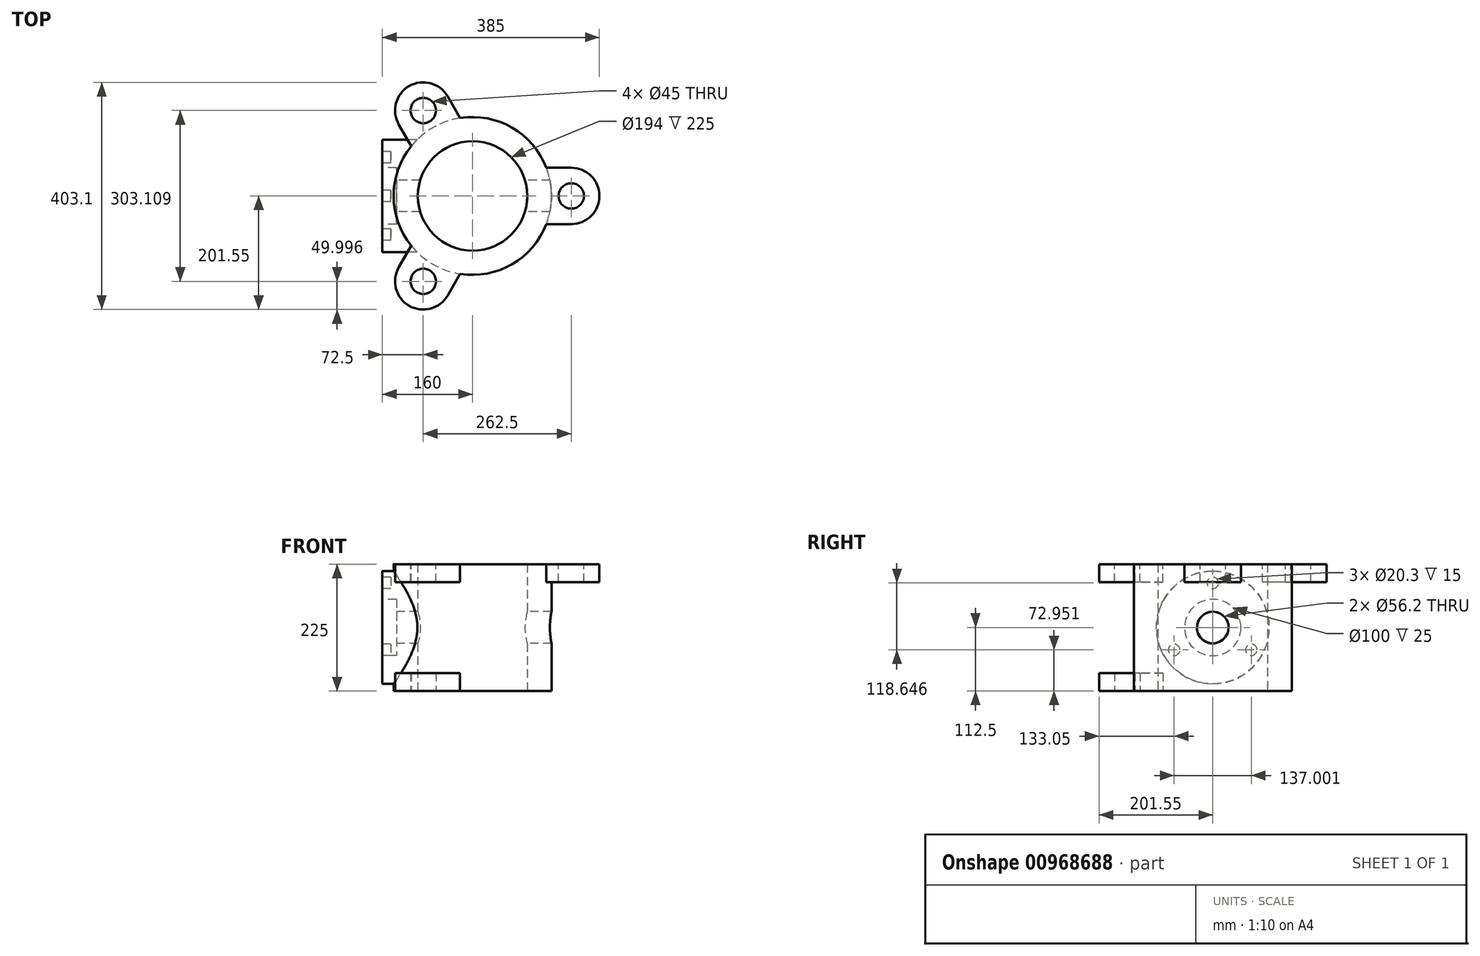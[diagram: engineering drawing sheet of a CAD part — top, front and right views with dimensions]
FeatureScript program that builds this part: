
annotation { "Feature Type Name" : "Feature", "Feature Type Description" : "" }
export const myFeature = defineFeature(function(context is Context, id is Id, definition is map)
    precondition{}
    {
        {
            var Q0;
            Q0=qCreatedBy(makeId("Top.planeOp"),FACE);
            var sketch = newSketch(context, id + "F0", { "sketchPlane" : qUnion([Q0])});
            skCircle(sketch, "E0", {"center": v(0, 0) * mm, "radius": 97 * mm});
            skCircle(sketch, "E1", {"center": v(0, 0) * mm, "radius": 140 * mm});
            skSolve(sketch);
        }
        {
            var Q0;
            Q0=makeQuery(id+"F0.imprint","IMPRINT",FACE,{"disambiguationData":[TD([[makeQuery(id+"F0.imprint","IMPRINT",EDGE,{"derivedFrom":sQuery(id+"F0.wireOp",EDGE,"E0")}),-1.0]])]});
            extrude(context, id + "F1", {"entities" : qUnion([Q0]), "endBound" : BoundingType.SYMMETRIC, "depth" : 225 * mm, "offsetDistance" : 25 * mm});
        }
        {
            var Q0;
            Q0=makeQuery(id+"F1.opExtrude","CAP_FACE",FACE,{"disambiguationData":[OSD([sQuery(id+"F0.wireOp",EDGE,"E0"),sQuery(id+"F0.wireOp",EDGE,"E1")])],"isStart":true});
            var sketch = newSketch(context, id + "F2", { "sketchPlane" : qUnion([Q0])});
            skLineSegment(sketch, "E2.0", {"start": v(-130.8, 126.55) * mm, "end": v(-108.68, 88.25) * mm});
            skArc(sketch, "E3.0", {"start": v(-130.8, 126.55) * mm, "mid": v(-112.5, 194.86) * mm, "end": v(-44.2, 176.55) * mm});
            skLineSegment(sketch, "E4.0", {"start": v(-44.2, 176.55) * mm, "end": v(-22.08, 138.25) * mm});
            skCircle(sketch, "E5.0", {"center": v(0, 0) * mm, "radius": 140 * mm});
            skCircle(sketch, "E6.0", {"center": v(-87.5, 151.55) * mm, "radius": 22.5 * mm});
            skSolve(sketch);
        }
        {
            var Q0;
            {var subQ1=sQuery(id+"F2FDXNzwOm2uh5E_1.2.F2.wireOp",EDGE,"E2.0");Q0=makeQuery(id+"F2FDXNzwOm2uh5E_1.2.F2.imprint","IMPRINT",FACE,{"disambiguationData":[TD([[makeQuery(id+"F2FDXNzwOm2uh5E_1.2.F2.imprint","IMPRINT",EDGE,{"derivedFrom":subQ1}),1.0]])]});}
            var Q1;
            {var subQ1=sQuery(id+"F2.wireOp",EDGE,"E2.0");Q1=makeQuery(id+"F2.imprint","IMPRINT",FACE,{"disambiguationData":[TD([[makeQuery(id+"F2.imprint","IMPRINT",EDGE,{"derivedFrom":subQ1}),1.0]])]});}
            var Q2;
            {var subQ1=sQuery(id+"F2FDXNzwOm2uh5E_1.1.F2.wireOp",EDGE,"E2.0");Q2=makeQuery(id+"F2FDXNzwOm2uh5E_1.1.F2.imprint","IMPRINT",FACE,{"disambiguationData":[TD([[makeQuery(id+"F2FDXNzwOm2uh5E_1.1.F2.imprint","IMPRINT",EDGE,{"derivedFrom":subQ1}),1.0]])]});}
            extrude(context, id + "F3", {"entities" : qUnion([Q0, Q1, Q2]), "operationType" : NewBodyOperationType.ADD, "oppositeDirection" : true, "depth" : 32 * mm, "offsetDistance" : 25 * mm});
        }
        {
            var Q0;
            Q0=qCreatedBy(makeId("Right.planeOp"),FACE);
            cPlane(context, id + "F4", {"entities" : qUnion([Q0]), "cplaneType" : CPlaneType.OFFSET, "offset" : 160 * mm, "oppositeDirection" : true, "width" : 150 * mm, "height" : 150 * mm});
        }
        {
            var Q0;
            Q0=qCreatedBy(id+"F4.planeOp",FACE);
            var sketch = newSketch(context, id + "F5", { "sketchPlane" : qUnion([Q0])});
            skCircle(sketch, "E7", {"center": v(0, 0) * mm, "radius": 100 * mm});
            skSolve(sketch);
        }
        {
            var Q0;
            Q0=makeQuery(id+"F5.imprint","IMPRINT",FACE,{"disambiguationData":[TD([[makeQuery(id+"F5.imprint","IMPRINT",EDGE,{"derivedFrom":sQuery(id+"F5.wireOp",EDGE,"E7")}),1.0]])]});
            extrude(context, id + "F6", {"entities" : qUnion([Q0]), "operationType" : NewBodyOperationType.ADD, "endBound" : BoundingType.UP_TO_NEXT, "depth" : 25 * mm, "offsetDistance" : 25 * mm});
        }
        {
            var Q0;
            Q0=makeQuery(id+"F6.opExtrude","CAP_FACE",FACE,{"disambiguationData":[OSD([sQuery(id+"F5.wireOp",EDGE,"E7")])],"isStart":true});
            var sketch = newSketch(context, id + "F7", { "sketchPlane" : qUnion([Q0])});
            skCircle(sketch, "E8", {"center": v(0, 0) * mm, "radius": 28.1 * mm});
            skSolve(sketch);
        }
        {
            var Q0;
            Q0=makeQuery(id+"F7.imprint","IMPRINT",FACE,{"disambiguationData":[TD([[makeQuery(id+"F7.imprint","IMPRINT",EDGE,{"derivedFrom":sQuery(id+"F7.wireOp",EDGE,"E8")}),1.0]])]});
            extrude(context, id + "F8", {"entities" : qUnion([Q0]), "operationType" : NewBodyOperationType.REMOVE, "oppositeDirection" : true, "depth" : 310 * mm, "offsetDistance" : 25 * mm});
        }
        {
            var Q0;
            Q0=makeQuery(id+"F6.opExtrude","CAP_FACE",FACE,{"disambiguationData":[OSD([sQuery(id+"F5.wireOp",EDGE,"E7")])],"isStart":true});
            var sketch = newSketch(context, id + "F9", { "sketchPlane" : qUnion([Q0])});
            skCircle(sketch, "E9", {"center": v(0, 0) * mm, "radius": 50 * mm});
            skSolve(sketch);
        }
        {
            var Q0;
            Q0=makeQuery(id+"F9.imprint","IMPRINT",FACE,{"disambiguationData":[TD([[makeQuery(id+"F9.imprint","IMPRINT",EDGE,{"derivedFrom":sQuery(id+"F9.wireOp",EDGE,"E9")}),1.0]])]});
            extrude(context, id + "F10", {"entities" : qUnion([Q0]), "operationType" : NewBodyOperationType.REMOVE, "oppositeDirection" : true, "depth" : 25 * mm, "offsetDistance" : 25 * mm});
        }
        {
            var Q0;
            Q0=makeQuery(id+"F9.imprint","IMPRINT",FACE,{"disambiguationData":[TD([[makeQuery(id+"F9.imprint","IMPRINT",EDGE,{"derivedFrom":sQuery(id+"F9.wireOp",EDGE,"E9")}),-1.0]])]});
            var sketch = newSketch(context, id + "F11", { "sketchPlane" : qUnion([Q0])});
            skCircle(sketch, "E10", {"center": v(0, 79.1) * mm, "radius": 10.15 * mm});
            skCircle(sketch, "E11.1.0", {"center": v(-68.5, -39.55) * mm, "radius": 10.15 * mm});
            skCircle(sketch, "E11.2.0", {"center": v(68.5, -39.55) * mm, "radius": 10.15 * mm});
            skPoint(sketch, "E11.center", {"position": v(0, 0) * mm});
            skSolve(sketch);
        }
        {
            var Q0;
            Q0 = qSketchRegion(id + "F11", true);
            extrude(context, id + "F12", {"entities" : qUnion([Q0]), "operationType" : NewBodyOperationType.REMOVE, "oppositeDirection" : true, "depth" : 15 * mm, "offsetDistance" : 25 * mm});
        }
        {
            var Q0;
            Q0=makeQuery(id+"F9.imprint","IMPRINT",FACE,{"disambiguationData":[TD([[makeQuery(id+"F9.imprint","IMPRINT",EDGE,{"derivedFrom":sQuery(id+"F9.wireOp",EDGE,"E9")}),-1.0]])]});
            var sketch = newSketch(context, id + "F13", { "sketchPlane" : qUnion([Q0])});
            skCircle(sketch, "E12.0", {"center": v(0, 0) * mm, "radius": 100 * mm});
            skCircle(sketch, "E13.0", {"center": v(0, 79.1) * mm, "radius": 10.15 * mm});
            skCircle(sketch, "E14.0", {"center": v(-68.5, -39.55) * mm, "radius": 10.15 * mm});
            skCircle(sketch, "E15.0", {"center": v(68.5, -39.55) * mm, "radius": 10.15 * mm});
            skSolve(sketch);
        }
        {
            var Q0;
            Q0=makeQuery(id+"F1.opExtrude","CAP_FACE",FACE,{"disambiguationData":[OSD([sQuery(id+"F0.wireOp",EDGE,"E0"),sQuery(id+"F0.wireOp",EDGE,"E1")])],"isStart":false});
            var sketch = newSketch(context, id + "F14", { "sketchPlane" : qUnion([Q0])});
            skArc(sketch, "E16.0", {"start": v(-108.68, 88.25) * mm, "mid": v(-70, 121.24) * mm, "end": v(-22.08, 138.25) * mm});
            skLineSegment(sketch, "E17.0", {"start": v(175, 50) * mm, "end": v(130.77, 50) * mm});
            skArc(sketch, "E18.0", {"start": v(175, -50) * mm, "mid": v(225, 0) * mm, "end": v(175, 50) * mm});
            skLineSegment(sketch, "E19.0", {"start": v(175, -50) * mm, "end": v(130.77, -50) * mm});
            skCircle(sketch, "E20.0", {"center": v(175, 0) * mm, "radius": 22.5 * mm});
            skPoint(sketch, "E21.0", {"position": v(-33.14, 157.4) * mm});
            skLineSegment(sketch, "E22.0", {"start": v(-44.2, 176.55) * mm, "end": v(-22.08, 138.25) * mm});
            skArc(sketch, "E23.0", {"start": v(-44.2, 176.55) * mm, "mid": v(-112.5, 194.86) * mm, "end": v(-130.8, 126.55) * mm});
            skPoint(sketch, "E24.0", {"position": v(-119.74, 107.4) * mm});
            skLineSegment(sketch, "E25.0", {"start": v(-130.8, 126.55) * mm, "end": v(-108.68, 88.25) * mm});
            skLineSegment(sketch, "E26.0", {"start": v(-130.8, -126.55) * mm, "end": v(-108.68, -88.25) * mm});
            skArc(sketch, "E27.0", {"start": v(-130.8, -126.55) * mm, "mid": v(-112.5, -194.86) * mm, "end": v(-44.2, -176.55) * mm});
            skLineSegment(sketch, "E28.0", {"start": v(-44.2, -176.55) * mm, "end": v(-22.08, -138.25) * mm});
            skArc(sketch, "E29.trimOffspring", {"start": v(130.77, 50) * mm, "mid": v(140, 0) * mm, "end": v(130.77, -50) * mm});
            skArc(sketch, "E30.trimOffspring", {"start": v(-22.08, -138.25) * mm, "mid": v(-70, -121.24) * mm, "end": v(-108.68, -88.25) * mm});
            skCircle(sketch, "E31.0", {"center": v(-87.5, 151.55) * mm, "radius": 22.5 * mm});
            skCircle(sketch, "E32.0", {"center": v(-87.5, -151.55) * mm, "radius": 22.5 * mm});
            skSolve(sketch);
        }
        {
            var Q0;
            Q0=makeQuery(id+"F14.imprint","IMPRINT",FACE,{"disambiguationData":[TD([[makeQuery(id+"F14.imprint","IMPRINT",EDGE,{"derivedFrom":sQuery(id+"F14.wireOp",EDGE,"E16.0")}),-1.0]])]});
            var Q1;
            Q1=makeQuery(id+"F14.imprint","IMPRINT",FACE,{"disambiguationData":[TD([[makeQuery(id+"F14.imprint","IMPRINT",EDGE,{"derivedFrom":sQuery(id+"F14.wireOp",EDGE,"E26.0")}),-1.0]])]});
            var Q2;
            Q2=makeQuery(id+"F14.imprint","IMPRINT",FACE,{"disambiguationData":[TD([[makeQuery(id+"F14.imprint","IMPRINT",EDGE,{"derivedFrom":sQuery(id+"F14.wireOp",EDGE,"E17.0")}),1.0]])]});
            extrude(context, id + "F15", {"entities" : qUnion([Q0, Q1, Q2]), "operationType" : NewBodyOperationType.ADD, "oppositeDirection" : true, "depth" : 32 * mm, "offsetDistance" : 25 * mm});
        }
    });
